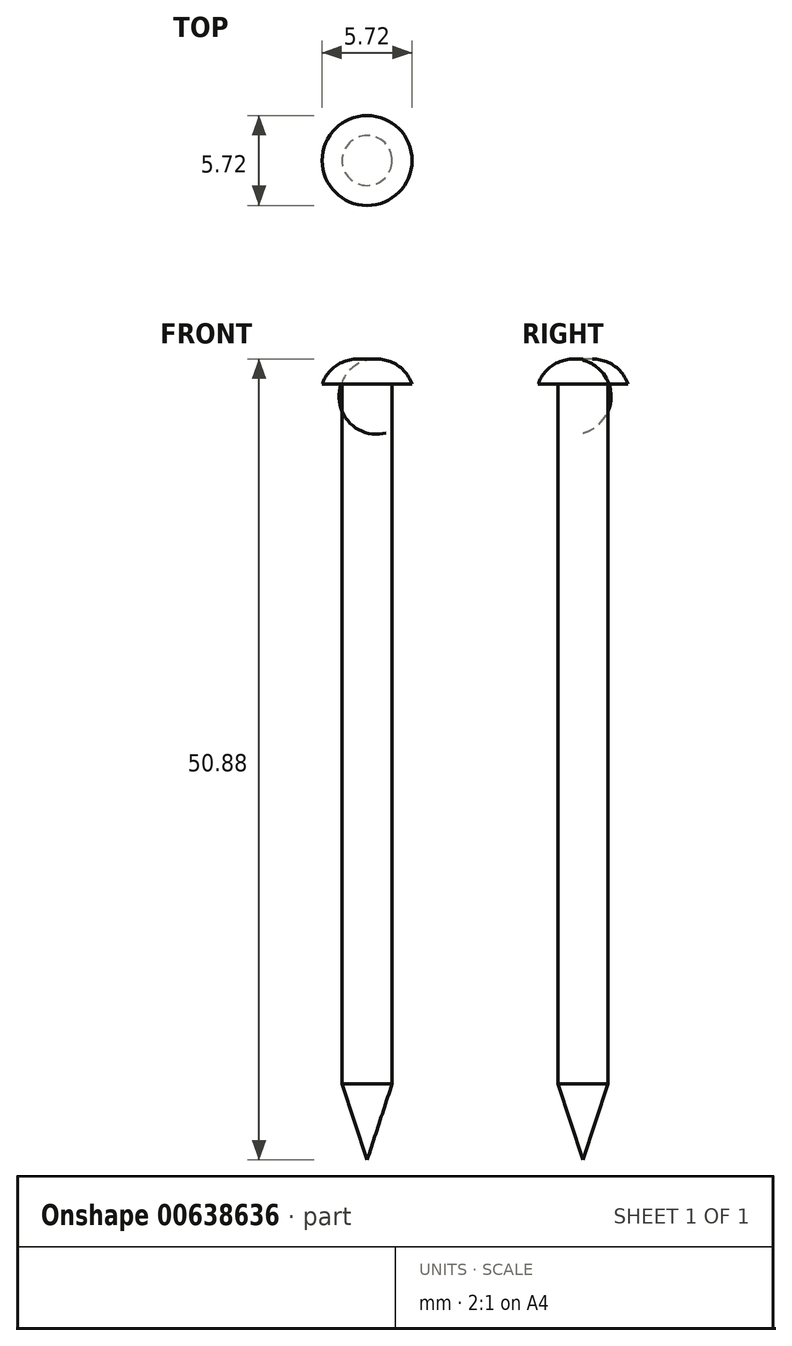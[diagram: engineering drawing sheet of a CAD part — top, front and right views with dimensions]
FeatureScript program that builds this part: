
annotation { "Feature Type Name" : "Feature", "Feature Type Description" : "" }
export const myFeature = defineFeature(function(context is Context, id is Id, definition is map)
    precondition{}
    {
        {
            var Q0;
            Q0=qCreatedBy(makeId("Front.planeOp"),FACE);
            var sketch = newSketch(context, id + "F0", { "sketchPlane" : qUnion([Q0])});
            skLineSegment(sketch, "E0", {"start": v(0, -29.84) * mm, "end": v(-1.59, -29.84) * mm});
            skLineSegment(sketch, "E1", {"start": v(-1.59, -29.84) * mm, "end": v(0, -34.67) * mm});
            skLineSegment(sketch, "E2", {"start": v(-1.59, -29.84) * mm, "end": v(-1.59, 14.61) * mm});
            skLineSegment(sketch, "E3", {"start": v(-1.59, 14.61) * mm, "end": v(-2.86, 14.61) * mm});
            skLineSegment(sketch, "E4", {"start": v(0, -34.67) * mm, "end": v(0, 16.13) * mm});
            skArc(sketch, "E5", {"start": v(0, 16.13) * mm, "mid": v(-1.73, 15.93) * mm, "end": v(-2.86, 14.61) * mm});
            skLineSegment(sketch, "E6", {"start": v(0, 22.3) * mm, "end": v(0, -39.93) * mm, "construction": true});
            skSolve(sketch);
        }
        {
            var Q0;
            Q0 = qSketchRegion(id + "F0", true);
            var Q1;
            Q1=sQuery(id+"F0.wireOp",EDGE,"E6");
            revolve(context, id + "F1", {"entities" : qUnion([Q0]), "axis" : qUnion([Q1]), "revolveType" : RevolveType.FULL});
        }
    });
